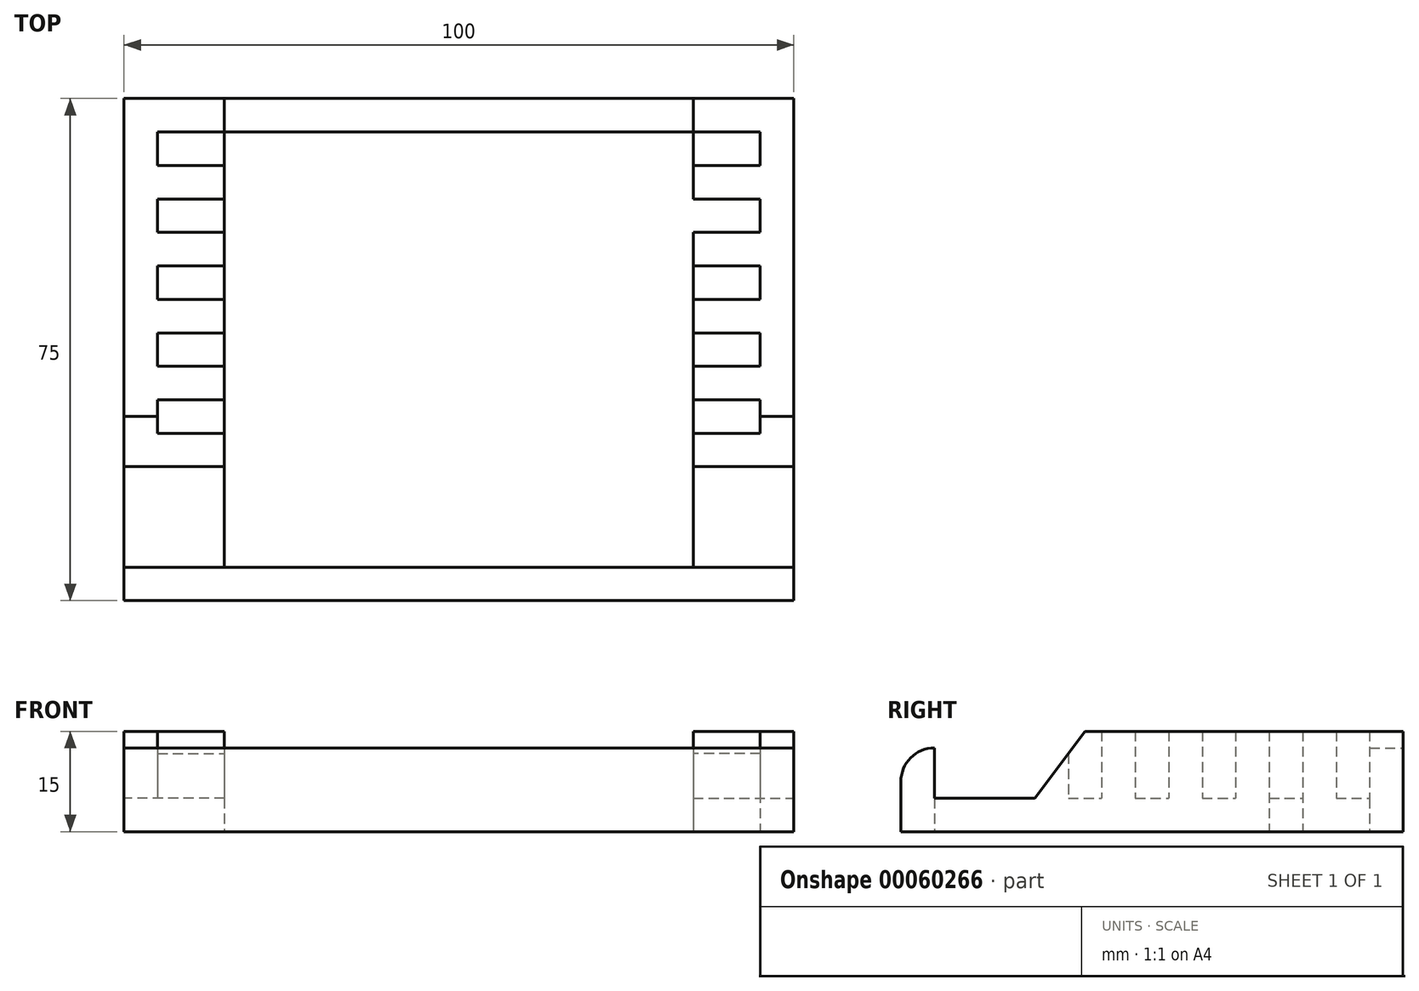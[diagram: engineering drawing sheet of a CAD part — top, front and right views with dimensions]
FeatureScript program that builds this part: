
annotation { "Feature Type Name" : "Feature", "Feature Type Description" : "" }
export const myFeature = defineFeature(function(context is Context, id is Id, definition is map)
    precondition{}
    {
        {
            var Q0;
            Q0=qCreatedBy(makeId("Top.planeOp"),FACE);
            var sketch = newSketch(context, id + "F0", { "sketchPlane" : qUnion([Q0])});
            skLineSegment(sketch, "E0.rect.top", {"start": v(-50, -40) * mm, "end": v(50, -40) * mm});
            skPoint(sketch, "E0.rect.middle", {"position": v(0, 0) * mm});
            skLineSegment(sketch, "E1.top", {"start": v(-50, -35) * mm, "end": v(50, -35) * mm});
            skLineSegment(sketch, "E1.left", {"start": v(-50, -40) * mm, "end": v(-50, -35) * mm});
            skLineSegment(sketch, "E1.right", {"start": v(50, -40) * mm, "end": v(50, -35) * mm});
            skPoint(sketch, "E2", {"position": v(50, -20) * mm});
            skPoint(sketch, "E3", {"position": v(50, -15) * mm});
            skPoint(sketch, "E4", {"position": v(50, -10) * mm});
            skPoint(sketch, "E5", {"position": v(50, -5) * mm});
            skPoint(sketch, "E6", {"position": v(50, 0) * mm});
            skLineSegment(sketch, "E7", {"start": v(50, -20) * mm, "end": v(50, -15) * mm});
            skLineSegment(sketch, "E8", {"start": v(50, -15) * mm, "end": v(50, -10) * mm});
            skLineSegment(sketch, "E9", {"start": v(35, -5) * mm, "end": v(45, -5) * mm});
            skLineSegment(sketch, "E10", {"start": v(45, -10) * mm, "end": v(35, -10) * mm});
            skLineSegment(sketch, "E11", {"start": v(45, -15) * mm, "end": v(35, -15) * mm});
            skLineSegment(sketch, "E12", {"start": v(35, -20) * mm, "end": v(45, -20) * mm});
            skLineSegment(sketch, "E13", {"start": v(-50, 35) * mm, "end": v(50, 35) * mm});
            skPoint(sketch, "E14", {"position": v(50, 5) * mm});
            skPoint(sketch, "E15", {"position": v(50, 10) * mm});
            skPoint(sketch, "E16", {"position": v(50, 15) * mm});
            skPoint(sketch, "E17", {"position": v(50, 20) * mm});
            skPoint(sketch, "E18", {"position": v(50, 25) * mm});
            skPoint(sketch, "E19", {"position": v(50, 30) * mm});
            skLineSegment(sketch, "E20", {"start": v(35, 25) * mm, "end": v(45, 25) * mm});
            skLineSegment(sketch, "E21.bottom", {"start": v(45, 20) * mm, "end": v(35, 20) * mm});
            skLineSegment(sketch, "E21.top", {"start": v(45, 20) * mm, "end": v(35, 20) * mm});
            skLineSegment(sketch, "E21.left", {"start": v(45, 20) * mm, "end": v(45, 20) * mm});
            skLineSegment(sketch, "E21.right", {"start": v(35, 20) * mm, "end": v(35, 20) * mm});
            skLineSegment(sketch, "E22", {"start": v(45, 15) * mm, "end": v(35, 15) * mm});
            skLineSegment(sketch, "E23", {"start": v(45, 10) * mm, "end": v(35, 10) * mm});
            skLineSegment(sketch, "E24", {"start": v(45, 5) * mm, "end": v(35, 5) * mm});
            skLineSegment(sketch, "E25", {"start": v(45, 0) * mm, "end": v(35, 0) * mm});
            skLineSegment(sketch, "E26", {"start": v(35, -35) * mm, "end": v(35, 35) * mm});
            skLineSegment(sketch, "E27", {"start": v(-35, -35) * mm, "end": v(-35, 35) * mm});
            skLineSegment(sketch, "E28", {"start": v(50, -35) * mm, "end": v(50, 35) * mm});
            skLineSegment(sketch, "E29", {"start": v(50, -20) * mm, "end": v(45, -20) * mm});
            skPoint(sketch, "E30", {"position": v(-45, -20) * mm});
            skLineSegment(sketch, "E31", {"start": v(-50, 35) * mm, "end": v(-50, -40) * mm});
            skPoint(sketch, "E32", {"position": v(-45, -15) * mm});
            skPoint(sketch, "E33", {"position": v(-45, -10) * mm});
            skPoint(sketch, "E34", {"position": v(-45, -5) * mm});
            skPoint(sketch, "E35", {"position": v(-45, 0) * mm});
            skPoint(sketch, "E36", {"position": v(-45, 5) * mm});
            skPoint(sketch, "E37", {"position": v(-45, 10) * mm});
            skPoint(sketch, "E38", {"position": v(-45, 15) * mm});
            skPoint(sketch, "E39", {"position": v(-45, 20) * mm});
            skPoint(sketch, "E40", {"position": v(-45, 25) * mm});
            skLineSegment(sketch, "E41", {"start": v(-45, -20) * mm, "end": v(-35, -20) * mm});
            skLineSegment(sketch, "E42", {"start": v(-45, -20) * mm, "end": v(-50, -20) * mm});
            skLineSegment(sketch, "E43", {"start": v(-45, -15) * mm, "end": v(-35, -15) * mm});
            skLineSegment(sketch, "E44", {"start": v(-45, -10) * mm, "end": v(-35, -10) * mm});
            skLineSegment(sketch, "E45", {"start": v(-45, -5) * mm, "end": v(-35, -5) * mm});
            skLineSegment(sketch, "E46", {"start": v(-45, 0) * mm, "end": v(-35, 0) * mm});
            skLineSegment(sketch, "E47", {"start": v(-45, 5) * mm, "end": v(-35, 5) * mm});
            skLineSegment(sketch, "E48", {"start": v(-45, 10) * mm, "end": v(-35, 10) * mm});
            skLineSegment(sketch, "E49", {"start": v(-45, 15) * mm, "end": v(-35, 15) * mm});
            skLineSegment(sketch, "E50", {"start": v(-45, 20) * mm, "end": v(-35, 20) * mm});
            skLineSegment(sketch, "E51", {"start": v(-45, 25) * mm, "end": v(-35, 25) * mm});
            skLineSegment(sketch, "E52", {"start": v(-45, -20) * mm, "end": v(-45, 30) * mm});
            skLineSegment(sketch, "E53", {"start": v(45, -20) * mm, "end": v(45, 30) * mm});
            skLineSegment(sketch, "E54", {"start": v(-45, 30) * mm, "end": v(-35, 30) * mm});
            skLineSegment(sketch, "E55", {"start": v(45, 30) * mm, "end": v(35, 30) * mm});
            skLineSegment(sketch, "E56", {"start": v(35, 30) * mm, "end": v(-35, 30) * mm});
            skSolve(sketch);
        }
        {
            var Q0;
            {var subQ4=sQuery(id+"F0.wireOp",EDGE,"E12");Q0=makeQuery(id+"F0.imprint","IMPRINT",FACE,{"disambiguationData":[TD([[makeQuery(id+"F0.imprint","IMPRINT",EDGE,{"derivedFrom":subQ4}),-1.0]])]});}
            var Q1;
            {var subQ0=sQuery(id+"F0.wireOp",EDGE,"E11");Q1=makeQuery(id+"F0.imprint","IMPRINT",FACE,{"disambiguationData":[TD([[makeQuery(id+"F0.imprint","IMPRINT",EDGE,{"derivedFrom":subQ0}),1.0]])]});}
            var Q2;
            {var subQ15=sQuery(id+"F0.wireOp",EDGE,"E29");Q2=makeQuery(id+"F0.imprint","IMPRINT",FACE,{"disambiguationData":[TD([[makeQuery(id+"F0.imprint","IMPRINT",EDGE,{"derivedFrom":subQ15}),-1.0]])]});}
            var Q3;
            {var subQ0=sQuery(id+"F0.wireOp",EDGE,"E10");Q3=makeQuery(id+"F0.imprint","IMPRINT",FACE,{"disambiguationData":[TD([[makeQuery(id+"F0.imprint","IMPRINT",EDGE,{"derivedFrom":subQ0}),1.0]])]});}
            var Q4;
            {var subQ0=sQuery(id+"F0.wireOp",EDGE,"E9");Q4=makeQuery(id+"F0.imprint","IMPRINT",FACE,{"disambiguationData":[TD([[makeQuery(id+"F0.imprint","IMPRINT",EDGE,{"derivedFrom":subQ0}),-1.0]])]});}
            var Q5;
            {var subQ0=sQuery(id+"F0.wireOp",EDGE,"E9");Q5=makeQuery(id+"F0.imprint","IMPRINT",FACE,{"disambiguationData":[TD([[makeQuery(id+"F0.imprint","IMPRINT",EDGE,{"derivedFrom":subQ0}),1.0]])]});}
            var Q6;
            {var subQ0=sQuery(id+"F0.wireOp",EDGE,"E24");Q6=makeQuery(id+"F0.imprint","IMPRINT",FACE,{"disambiguationData":[TD([[makeQuery(id+"F0.imprint","IMPRINT",EDGE,{"derivedFrom":subQ0}),1.0]])]});}
            var Q7;
            {var subQ0=sQuery(id+"F0.wireOp",EDGE,"E23");Q7=makeQuery(id+"F0.imprint","IMPRINT",FACE,{"disambiguationData":[TD([[makeQuery(id+"F0.imprint","IMPRINT",EDGE,{"derivedFrom":subQ0}),1.0]])]});}
            var Q8;
            {var subQ0=sQuery(id+"F0.wireOp",EDGE,"E22");Q8=makeQuery(id+"F0.imprint","IMPRINT",FACE,{"disambiguationData":[TD([[makeQuery(id+"F0.imprint","IMPRINT",EDGE,{"derivedFrom":subQ0}),1.0]])]});}
            var Q9;
            {var subQ0=sQuery(id+"F0.wireOp",EDGE,"E21.top");Q9=makeQuery(id+"F0.imprint","IMPRINT",FACE,{"disambiguationData":[TD([[makeQuery(id+"F0.imprint","IMPRINT",EDGE,{"derivedFrom":subQ0}),1.0]])]});}
            var Q10;
            {var subQ0=sQuery(id+"F0.wireOp",EDGE,"E20");Q10=makeQuery(id+"F0.imprint","IMPRINT",FACE,{"disambiguationData":[TD([[makeQuery(id+"F0.imprint","IMPRINT",EDGE,{"derivedFrom":subQ0}),-1.0]])]});}
            var Q11;
            {var subQ0=sQuery(id+"F0.wireOp",EDGE,"E20");Q11=makeQuery(id+"F0.imprint","IMPRINT",FACE,{"disambiguationData":[TD([[makeQuery(id+"F0.imprint","IMPRINT",EDGE,{"derivedFrom":subQ0}),1.0]])]});}
            extrude(context, id + "F1", {"entities" : qUnion([Q0, Q1, Q2, Q3, Q4, Q5, Q6, Q7, Q8, Q9, Q10, Q11]), "depth" : 5 * mm});
        }
        {
            var Q0;
            {var subQ5=sQuery(id+"F0.wireOp",EDGE,"E0.rect.top");Q0=makeQuery(id+"F0.imprint","IMPRINT",FACE,{"disambiguationData":[TD([[makeQuery(id+"F0.imprint","IMPRINT",EDGE,{"derivedFrom":subQ5}),1.0]])]});}
            var Q1;
            {var subQ5=sQuery(id+"F0.wireOp",EDGE,"E56");Q1=makeQuery(id+"F0.imprint","IMPRINT",FACE,{"disambiguationData":[TD([[makeQuery(id+"F0.imprint","IMPRINT",EDGE,{"derivedFrom":subQ5}),-1.0]])]});}
            extrude(context, id + "F2", {"entities" : qUnion([Q0, Q1]), "operationType" : NewBodyOperationType.ADD, "depth" : 12.5 * mm});
        }
        {
            var Q0;
            {var subQ6=sQuery(id+"F0.wireOp",EDGE,"E41");Q0=makeQuery(id+"F0.imprint","IMPRINT",FACE,{"disambiguationData":[TD([[makeQuery(id+"F0.imprint","IMPRINT",EDGE,{"derivedFrom":subQ6}),-1.0]])]});}
            var Q1;
            {var subQ0=sQuery(id+"F0.wireOp",EDGE,"E41");Q1=makeQuery(id+"F0.imprint","IMPRINT",FACE,{"disambiguationData":[TD([[makeQuery(id+"F0.imprint","IMPRINT",EDGE,{"derivedFrom":subQ0}),1.0]])]});}
            var Q2;
            {var subQ0=sQuery(id+"F0.wireOp",EDGE,"E43");Q2=makeQuery(id+"F0.imprint","IMPRINT",FACE,{"disambiguationData":[TD([[makeQuery(id+"F0.imprint","IMPRINT",EDGE,{"derivedFrom":subQ0}),1.0]])]});}
            var Q3;
            {var subQ0=sQuery(id+"F0.wireOp",EDGE,"E44");Q3=makeQuery(id+"F0.imprint","IMPRINT",FACE,{"disambiguationData":[TD([[makeQuery(id+"F0.imprint","IMPRINT",EDGE,{"derivedFrom":subQ0}),1.0]])]});}
            var Q4;
            {var subQ0=sQuery(id+"F0.wireOp",EDGE,"E45");Q4=makeQuery(id+"F0.imprint","IMPRINT",FACE,{"disambiguationData":[TD([[makeQuery(id+"F0.imprint","IMPRINT",EDGE,{"derivedFrom":subQ0}),1.0]])]});}
            var Q5;
            {var subQ0=sQuery(id+"F0.wireOp",EDGE,"E46");Q5=makeQuery(id+"F0.imprint","IMPRINT",FACE,{"disambiguationData":[TD([[makeQuery(id+"F0.imprint","IMPRINT",EDGE,{"derivedFrom":subQ0}),1.0]])]});}
            var Q6;
            {var subQ0=sQuery(id+"F0.wireOp",EDGE,"E47");Q6=makeQuery(id+"F0.imprint","IMPRINT",FACE,{"disambiguationData":[TD([[makeQuery(id+"F0.imprint","IMPRINT",EDGE,{"derivedFrom":subQ0}),1.0]])]});}
            var Q7;
            {var subQ0=sQuery(id+"F0.wireOp",EDGE,"E48");Q7=makeQuery(id+"F0.imprint","IMPRINT",FACE,{"disambiguationData":[TD([[makeQuery(id+"F0.imprint","IMPRINT",EDGE,{"derivedFrom":subQ0}),1.0]])]});}
            var Q8;
            {var subQ0=sQuery(id+"F0.wireOp",EDGE,"E49");Q8=makeQuery(id+"F0.imprint","IMPRINT",FACE,{"disambiguationData":[TD([[makeQuery(id+"F0.imprint","IMPRINT",EDGE,{"derivedFrom":subQ0}),1.0]])]});}
            var Q9;
            {var subQ0=sQuery(id+"F0.wireOp",EDGE,"E50");Q9=makeQuery(id+"F0.imprint","IMPRINT",FACE,{"disambiguationData":[TD([[makeQuery(id+"F0.imprint","IMPRINT",EDGE,{"derivedFrom":subQ0}),1.0]])]});}
            var Q10;
            {var subQ0=sQuery(id+"F0.wireOp",EDGE,"E51");Q10=makeQuery(id+"F0.imprint","IMPRINT",FACE,{"disambiguationData":[TD([[makeQuery(id+"F0.imprint","IMPRINT",EDGE,{"derivedFrom":subQ0}),1.0]])]});}
            var Q11;
            {var subQ4=sQuery(id+"F0.wireOp",EDGE,"E42");Q11=makeQuery(id+"F0.imprint","IMPRINT",FACE,{"disambiguationData":[TD([[makeQuery(id+"F0.imprint","IMPRINT",EDGE,{"derivedFrom":subQ4}),-1.0]])]});}
            extrude(context, id + "F3", {"entities" : qUnion([Q0, Q1, Q2, Q3, Q4, Q5, Q6, Q7, Q8, Q9, Q10, Q11]), "operationType" : NewBodyOperationType.ADD, "depth" : 5 * mm});
        }
        {
            var Q0;
            {var subQ15=sQuery(id+"F0.wireOp",EDGE,"E29");Q0=makeQuery(id+"F0.imprint","IMPRINT",FACE,{"disambiguationData":[TD([[makeQuery(id+"F0.imprint","IMPRINT",EDGE,{"derivedFrom":subQ15}),-1.0]])]});}
            var Q1;
            {var subQ0=sQuery(id+"F0.wireOp",EDGE,"E11");Q1=makeQuery(id+"F0.imprint","IMPRINT",FACE,{"disambiguationData":[TD([[makeQuery(id+"F0.imprint","IMPRINT",EDGE,{"derivedFrom":subQ0}),1.0]])]});}
            var Q2;
            {var subQ0=sQuery(id+"F0.wireOp",EDGE,"E9");Q2=makeQuery(id+"F0.imprint","IMPRINT",FACE,{"disambiguationData":[TD([[makeQuery(id+"F0.imprint","IMPRINT",EDGE,{"derivedFrom":subQ0}),-1.0]])]});}
            var Q3;
            {var subQ0=sQuery(id+"F0.wireOp",EDGE,"E24");Q3=makeQuery(id+"F0.imprint","IMPRINT",FACE,{"disambiguationData":[TD([[makeQuery(id+"F0.imprint","IMPRINT",EDGE,{"derivedFrom":subQ0}),1.0]])]});}
            var Q4;
            {var subQ0=sQuery(id+"F0.wireOp",EDGE,"E22");Q4=makeQuery(id+"F0.imprint","IMPRINT",FACE,{"disambiguationData":[TD([[makeQuery(id+"F0.imprint","IMPRINT",EDGE,{"derivedFrom":subQ0}),1.0]])]});}
            var Q5;
            {var subQ0=sQuery(id+"F0.wireOp",EDGE,"E20");Q5=makeQuery(id+"F0.imprint","IMPRINT",FACE,{"disambiguationData":[TD([[makeQuery(id+"F0.imprint","IMPRINT",EDGE,{"derivedFrom":subQ0}),-1.0]])]});}
            extrude(context, id + "F4", {"entities" : qUnion([Q0, Q1, Q2, Q3, Q4, Q5]), "operationType" : NewBodyOperationType.ADD, "depth" : 15 * mm});
        }
        {
            var Q0;
            {var subQ0=sQuery(id+"F0.wireOp",EDGE,"E41");Q0=makeQuery(id+"F0.imprint","IMPRINT",FACE,{"disambiguationData":[TD([[makeQuery(id+"F0.imprint","IMPRINT",EDGE,{"derivedFrom":subQ0}),1.0]])]});}
            var Q1;
            {var subQ0=sQuery(id+"F0.wireOp",EDGE,"E44");Q1=makeQuery(id+"F0.imprint","IMPRINT",FACE,{"disambiguationData":[TD([[makeQuery(id+"F0.imprint","IMPRINT",EDGE,{"derivedFrom":subQ0}),1.0]])]});}
            var Q2;
            {var subQ0=sQuery(id+"F0.wireOp",EDGE,"E46");Q2=makeQuery(id+"F0.imprint","IMPRINT",FACE,{"disambiguationData":[TD([[makeQuery(id+"F0.imprint","IMPRINT",EDGE,{"derivedFrom":subQ0}),1.0]])]});}
            var Q3;
            {var subQ0=sQuery(id+"F0.wireOp",EDGE,"E48");Q3=makeQuery(id+"F0.imprint","IMPRINT",FACE,{"disambiguationData":[TD([[makeQuery(id+"F0.imprint","IMPRINT",EDGE,{"derivedFrom":subQ0}),1.0]])]});}
            var Q4;
            {var subQ0=sQuery(id+"F0.wireOp",EDGE,"E50");Q4=makeQuery(id+"F0.imprint","IMPRINT",FACE,{"disambiguationData":[TD([[makeQuery(id+"F0.imprint","IMPRINT",EDGE,{"derivedFrom":subQ0}),1.0]])]});}
            var Q5;
            {var subQ4=sQuery(id+"F0.wireOp",EDGE,"E42");Q5=makeQuery(id+"F0.imprint","IMPRINT",FACE,{"disambiguationData":[TD([[makeQuery(id+"F0.imprint","IMPRINT",EDGE,{"derivedFrom":subQ4}),-1.0]])]});}
            extrude(context, id + "F5", {"entities" : qUnion([Q0, Q1, Q2, Q3, Q4, Q5]), "operationType" : NewBodyOperationType.ADD, "depth" : 15 * mm});
        }
        {
            var Q0;
            Q0=makeQuery(id+"F4.opExtrude","CAP_EDGE",EDGE,{"disambiguationData":[OSD([sQuery(id+"F0.wireOp",EDGE,"E12"),sQuery(id+"F0.wireOp",EDGE,"E29")])],"isStart":false});
            chamfer(context, id + "F6", {"entities" : qUnion([Q0]), "chamferType" : ChamferType.TWO_OFFSETS, "width1" : 10 * mm, "oppositeDirection" : false, "width2" : 7.5 * mm});
        }
        {
            var Q0;
            Q0=makeQuery(id+"F5.opExtrude","CAP_EDGE",EDGE,{"disambiguationData":[OSD([sQuery(id+"F0.wireOp",EDGE,"E41"),sQuery(id+"F0.wireOp",EDGE,"E42")])],"isStart":false});
            chamfer(context, id + "F7", {"entities" : qUnion([Q0]), "chamferType" : ChamferType.TWO_OFFSETS, "width1" : 7.5 * mm, "oppositeDirection" : false, "width2" : 10 * mm, "tangentPropagation" : true});
        }
        {
            var Q0;
            Q0=makeQuery(id+"F2.opExtrude","CAP_EDGE",EDGE,{"disambiguationData":[OSD([sQuery(id+"F0.wireOp",EDGE,"E0.rect.top")])],"isStart":false});
            fillet(context, id + "F8", {"entities" : qUnion([Q0]), "radius" : 5 * mm, "tangentPropagation" : true, "allowEdgeOverflow" : false});
        }
    });
